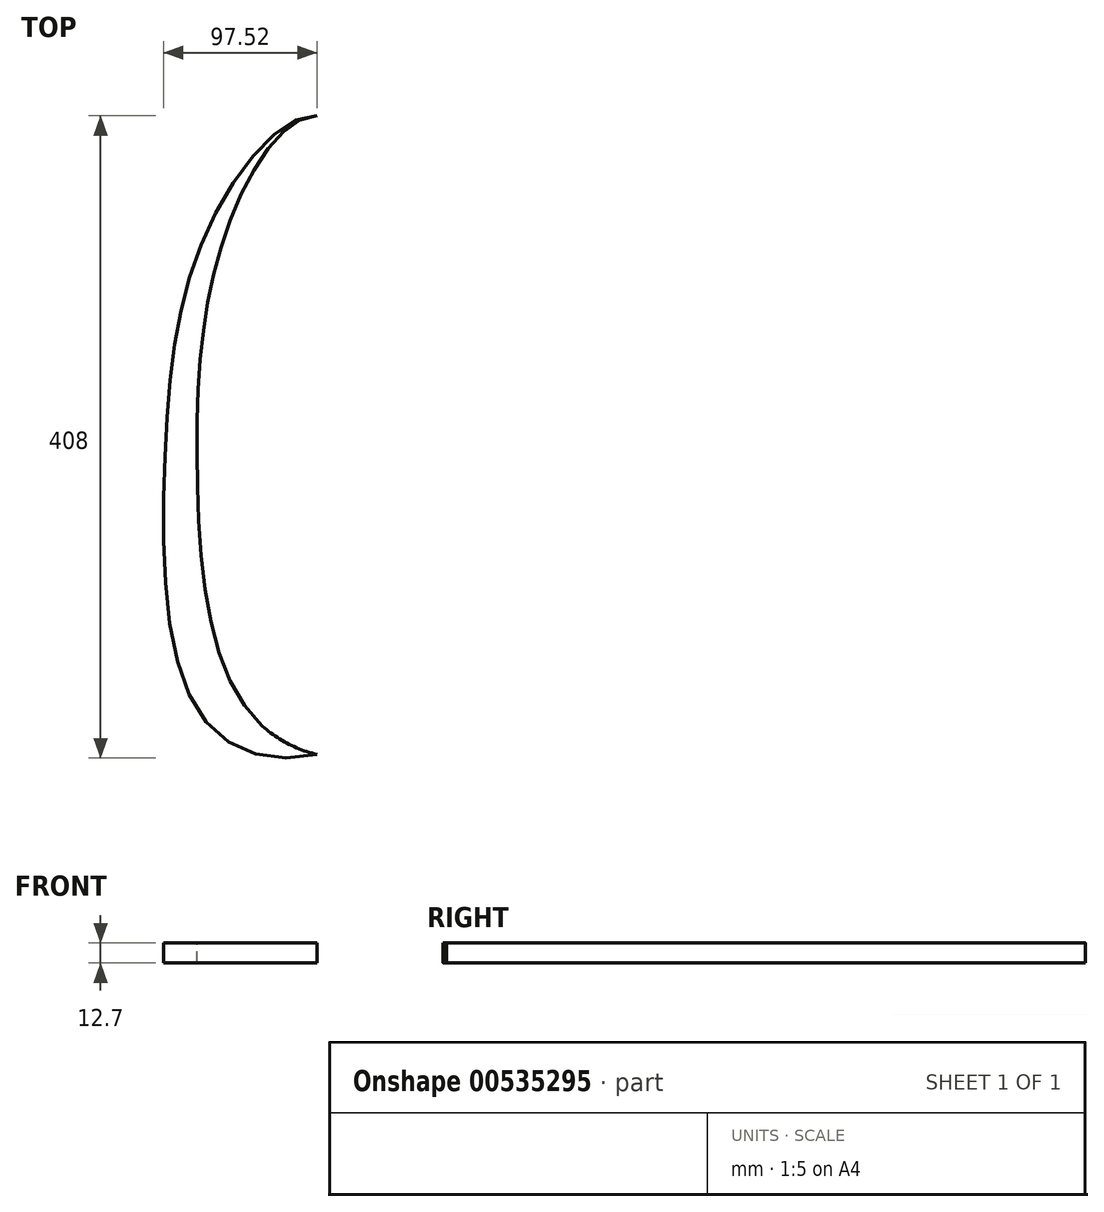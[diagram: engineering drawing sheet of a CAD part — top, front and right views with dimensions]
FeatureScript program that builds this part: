
annotation { "Feature Type Name" : "Feature", "Feature Type Description" : "" }
export const myFeature = defineFeature(function(context is Context, id is Id, definition is map)
    precondition{}
    {
        {
            var Q0;
            Q0=qCreatedBy(makeId("Top.planeOp"),FACE);
            var sketch = newSketch(context, id + "F0", { "sketchPlane" : qUnion([Q0])});
            skPoint(sketch, "E0.middle", {"position": v(0, 0) * mm});
            skFitSpline(sketch, "E1", {"points": [v(-479.8, 239.73) * mm, v(-422.83, 168.26) * mm, v(-403.6, 16.52) * mm, v(-444.99, -147.8) * mm, v(-543.61, -152.44) * mm, v(-576.7, 14.38) * mm, v(-548.93, 168.26) * mm, v(-479.8, 239.73) * mm]});
            skFitSpline(sketch, "E2.MirrorC", {"points": [v(-479.8, 239.73) * mm, v(-536.76, 168.26) * mm, v(-556, 16.52) * mm, v(-514.6, -147.8) * mm, v(-415.98, -152.44) * mm, v(-382.88, 14.38) * mm, v(-410.67, 168.26) * mm, v(-479.8, 239.73) * mm]});
            skPoint(sketch, "E0.top.end.orphan", {"position": v(-146.17, -365.42) * mm});
            skPoint(sketch, "E0.top.start.orphan", {"position": v(146.17, -365.42) * mm});
            skPoint(sketch, "E0.bottom.end.orphan", {"position": v(-146.17, 365.42) * mm});
            skPoint(sketch, "E0.bottom.start.orphan", {"position": v(146.17, 365.42) * mm});
            skLineSegment(sketch, "E3", {"start": v(-514.6, -147.8) * mm, "end": v(-481.29, -101.84) * mm});
            skLineSegment(sketch, "E4", {"start": v(-481.29, -101.84) * mm, "end": v(-444.99, -147.8) * mm});
            skPoint(sketch, "E5.orphan", {"position": v(-479.8, -165.97) * mm});
            skSolve(sketch);
        }
        {
            var Q0;
            Q0=makeQuery(id+"F0.imprint","IMPRINT",FACE,{"disambiguationData":[TD([[makeQuery(id+"F0.imprint","IMPRINT",EDGE,{"derivedFrom":sQuery(id+"F0.wireOp",EDGE,"E1")}),-1.0]])]});
            extrude(context, id + "F1", {"entities" : qUnion([Q0]), "depth" : 12.7 * mm, "offsetDistance" : 25.4 * mm});
        }
    });
